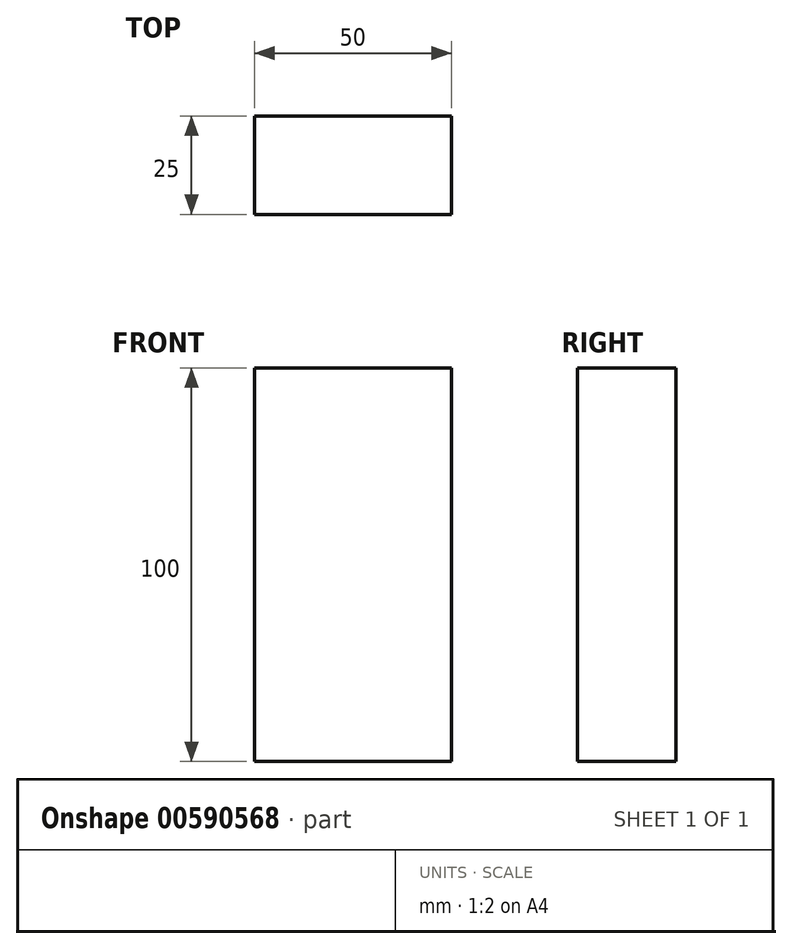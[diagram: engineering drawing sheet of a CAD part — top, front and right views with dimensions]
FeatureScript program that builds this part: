
annotation { "Feature Type Name" : "Feature", "Feature Type Description" : "" }
export const myFeature = defineFeature(function(context is Context, id is Id, definition is map)
    precondition{}
    {
        {
            var Q0;
            Q0=qCreatedBy(makeId("Top.planeOp"),FACE);
            var sketch = newSketch(context, id + "F0", { "sketchPlane" : qUnion([Q0])});
            skLineSegment(sketch, "E0.bottom", {"start": v(25, 12.5) * mm, "end": v(-25, 12.5) * mm});
            skLineSegment(sketch, "E0.top", {"start": v(25, -12.5) * mm, "end": v(-25, -12.5) * mm});
            skLineSegment(sketch, "E0.left", {"start": v(25, 12.5) * mm, "end": v(25, -12.5) * mm});
            skLineSegment(sketch, "E0.right", {"start": v(-25, 12.5) * mm, "end": v(-25, -12.5) * mm});
            skPoint(sketch, "E0.middle", {"position": v(0, 0) * mm});
            skSolve(sketch);
        }
        {
            var Q0;
            Q0=makeQuery(id+"F0.imprint","IMPRINT",FACE,{"disambiguationData":[TD([[makeQuery(id+"F0.imprint","IMPRINT",EDGE,{"derivedFrom":sQuery(id+"F0.wireOp",EDGE,"E0.bottom")}),1.0]])]});
            extrude(context, id + "F1", {"entities" : qUnion([Q0]), "depth" : 100 * mm, "offsetDistance" : 25 * mm});
        }
    });
